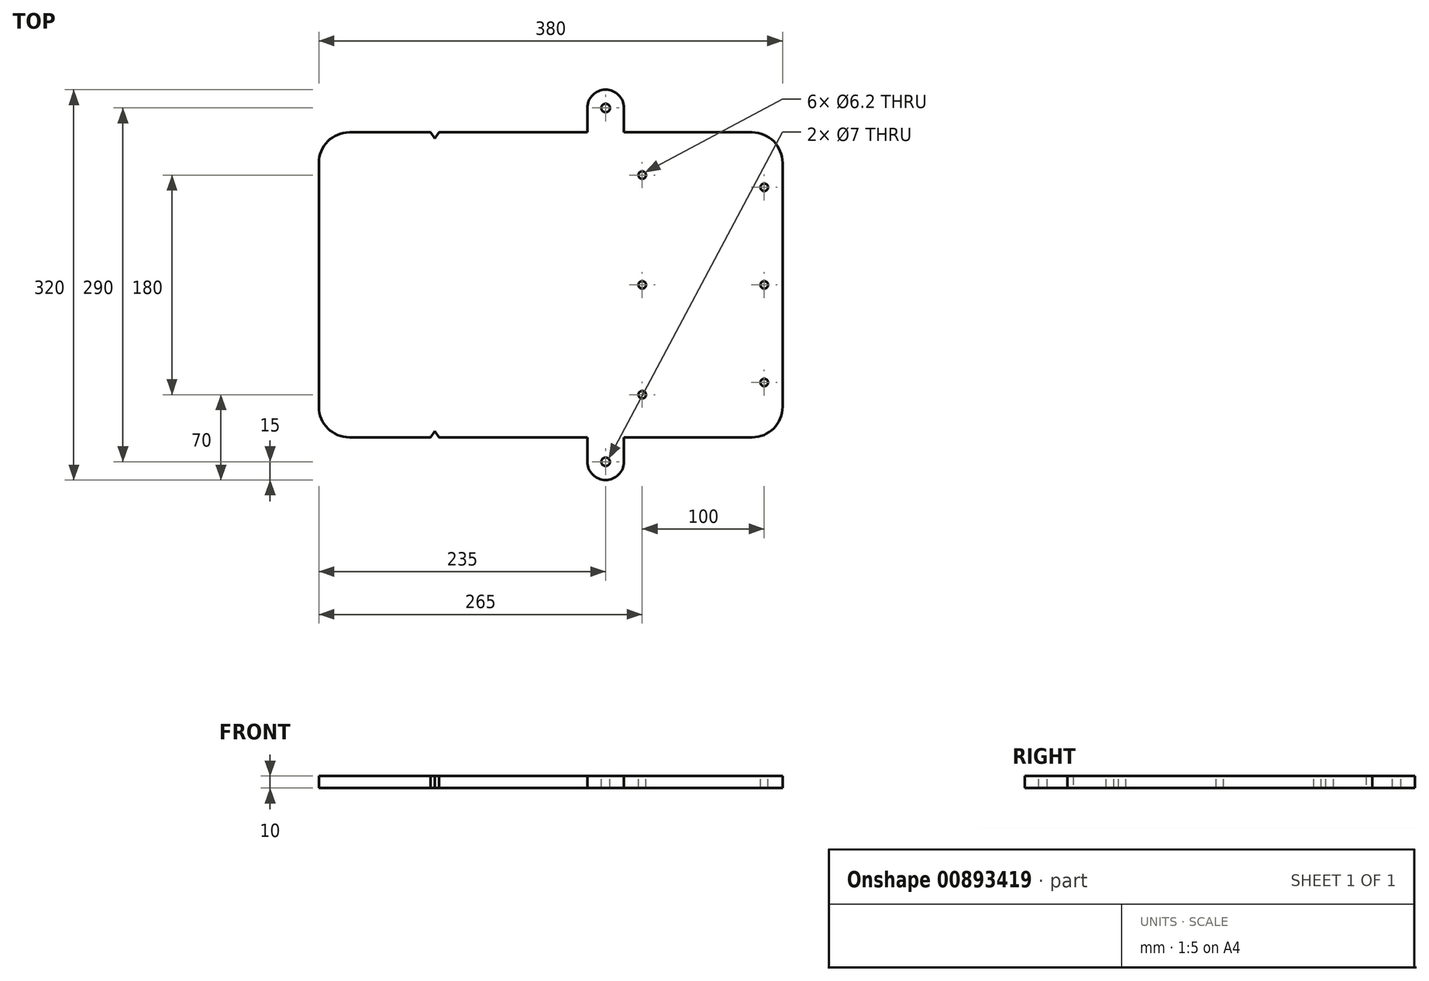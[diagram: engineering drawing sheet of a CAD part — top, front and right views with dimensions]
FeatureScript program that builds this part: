
annotation { "Feature Type Name" : "Feature", "Feature Type Description" : "" }
export const myFeature = defineFeature(function(context is Context, id is Id, definition is map)
    precondition{}
    {
        {
            var Q0;
            Q0=qCreatedBy(makeId("Top.planeOp"),FACE);
            var sketch = newSketch(context, id + "F0", { "sketchPlane" : qUnion([Q0])});
            skLineSegment(sketch, "E0.bottom", {"start": v(25, 0) * mm, "end": v(91.56, 0) * mm});
            skLineSegment(sketch, "E0.top", {"start": v(25, 250) * mm, "end": v(91.56, 250) * mm});
            skLineSegment(sketch, "E0.left", {"start": v(0, 25) * mm, "end": v(0, 225) * mm});
            skLineSegment(sketch, "E0.right", {"start": v(380, 25) * mm, "end": v(380, 225) * mm});
            skLineSegment(sketch, "E1.top", {"start": v(235, 285) * mm, "end": v(235, 285) * mm});
            skLineSegment(sketch, "E1.left", {"start": v(220, 250) * mm, "end": v(220, 270) * mm});
            skLineSegment(sketch, "E1.right", {"start": v(250, 250) * mm, "end": v(250, 270) * mm});
            skLineSegment(sketch, "E2.top", {"start": v(235, -35) * mm, "end": v(235, -35) * mm});
            skLineSegment(sketch, "E2.left", {"start": v(250, 0) * mm, "end": v(250, -20) * mm});
            skLineSegment(sketch, "E2.right", {"start": v(220, 0) * mm, "end": v(220, -20) * mm});
            skLineSegment(sketch, "E3.trimOffspring", {"start": v(250, 250) * mm, "end": v(355, 250) * mm});
            skLineSegment(sketch, "E4.trimOffspring", {"start": v(250, 0) * mm, "end": v(355, 0) * mm});
            skPoint(sketch, "E5.visualSharp", {"position": v(220, 285) * mm});
            skArc(sketch, "E5.filletArc", {"start": v(235, 285) * mm, "mid": v(224.4, 280.6) * mm, "end": v(220, 270) * mm});
            skPoint(sketch, "E6.visualSharp", {"position": v(250, 285) * mm});
            skArc(sketch, "E6.filletArc", {"start": v(250, 270) * mm, "mid": v(245.6, 280.6) * mm, "end": v(235, 285) * mm});
            skPoint(sketch, "E7.visualSharp", {"position": v(220, -35) * mm});
            skArc(sketch, "E7.filletArc", {"start": v(220, -20) * mm, "mid": v(224.4, -30.6) * mm, "end": v(235, -35) * mm});
            skPoint(sketch, "E8.visualSharp", {"position": v(250, -35) * mm});
            skArc(sketch, "E8.filletArc", {"start": v(235, -35) * mm, "mid": v(245.6, -30.6) * mm, "end": v(250, -20) * mm});
            skPoint(sketch, "E9.visualSharp", {"position": v(0, 250) * mm});
            skArc(sketch, "E9.filletArc", {"start": v(25, 250) * mm, "mid": v(7.32, 242.68) * mm, "end": v(0, 225) * mm});
            skPoint(sketch, "E10.visualSharp", {"position": v(0, 0) * mm});
            skArc(sketch, "E10.filletArc", {"start": v(0, 25) * mm, "mid": v(7.32, 7.32) * mm, "end": v(25, 0) * mm});
            skPoint(sketch, "E11.visualSharp", {"position": v(380, 0) * mm});
            skArc(sketch, "E11.filletArc", {"start": v(355, 0) * mm, "mid": v(372.68, 7.32) * mm, "end": v(380, 25) * mm});
            skPoint(sketch, "E12.visualSharp", {"position": v(380, 250) * mm});
            skArc(sketch, "E12.filletArc", {"start": v(380, 225) * mm, "mid": v(372.68, 242.68) * mm, "end": v(355, 250) * mm});
            skLineSegment(sketch, "E13", {"start": v(98.44, 250) * mm, "end": v(95, 245) * mm});
            skLineSegment(sketch, "E14", {"start": v(95, 245) * mm, "end": v(91.56, 250) * mm});
            skLineSegment(sketch, "E15.trimOffspring", {"start": v(98.44, 250) * mm, "end": v(220, 250) * mm});
            skLineSegment(sketch, "E16.MirrorCS", {"start": v(98.44, 0) * mm, "end": v(95, 5) * mm});
            skLineSegment(sketch, "E17.MirrorCS", {"start": v(95, 5) * mm, "end": v(91.56, 0) * mm});
            skLineSegment(sketch, "E18.trimOffspring", {"start": v(98.44, 0) * mm, "end": v(220, 0) * mm});
            skPoint(sketch, "E19.end.orphan", {"position": v(380, 125) * mm});
            skPoint(sketch, "E19.start.orphan", {"position": v(0, 125) * mm});
            skSolve(sketch);
        }
        {
            var Q0;
            Q0=makeQuery(id+"F0.imprint","IMPRINT",FACE,{"disambiguationData":[TD([[makeQuery(id+"F0.imprint","IMPRINT",EDGE,{"derivedFrom":sQuery(id+"F0.wireOp",EDGE,"E0.bottom")}),1.0]])]});
            extrude(context, id + "F1", {"entities" : qUnion([Q0]), "depth" : 10 * mm, "offsetDistance" : 25 * mm});
        }
        {
            var Q0;
            Q0=makeQuery(id+"F1.opExtrude","CAP_FACE",FACE,{"disambiguationData":[OSD([sQuery(id+"F0.wireOp",EDGE,"E0.bottom"),sQuery(id+"F0.wireOp",EDGE,"E0.top"),sQuery(id+"F0.wireOp",EDGE,"E0.left"),sQuery(id+"F0.wireOp",EDGE,"E0.right"),sQuery(id+"F0.wireOp",EDGE,"E1.left"),sQuery(id+"F0.wireOp",EDGE,"E1.right"),sQuery(id+"F0.wireOp",EDGE,"E2.left"),sQuery(id+"F0.wireOp",EDGE,"E2.right"),sQuery(id+"F0.wireOp",EDGE,"E3.trimOffspring"),sQuery(id+"F0.wireOp",EDGE,"E4.trimOffspring"),sQuery(id+"F0.wireOp",EDGE,"E5.filletArc"),sQuery(id+"F0.wireOp",EDGE,"E6.filletArc"),sQuery(id+"F0.wireOp",EDGE,"E7.filletArc"),sQuery(id+"F0.wireOp",EDGE,"E8.filletArc"),sQuery(id+"F0.wireOp",EDGE,"E9.filletArc"),sQuery(id+"F0.wireOp",EDGE,"E10.filletArc"),sQuery(id+"F0.wireOp",EDGE,"E11.filletArc"),sQuery(id+"F0.wireOp",EDGE,"E12.filletArc")])],"isStart":false});
            var sketch = newSketch(context, id + "F2", { "sketchPlane" : qUnion([Q0])});
            skCircle(sketch, "E20", {"center": v(235, 270) * mm, "radius": 3.5 * mm});
            skCircle(sketch, "E21", {"center": v(235, -20) * mm, "radius": 3.5 * mm});
            skSolve(sketch);
        }
        {
            var Q0;
            Q0=makeQuery(id+"F2.imprint","IMPRINT",FACE,{"disambiguationData":[TD([[makeQuery(id+"F2.imprint","IMPRINT",EDGE,{"derivedFrom":sQuery(id+"F2.wireOp",EDGE,"E21")}),1.0]])]});
            var Q1;
            Q1=makeQuery(id+"F2.imprint","IMPRINT",FACE,{"disambiguationData":[TD([[makeQuery(id+"F2.imprint","IMPRINT",EDGE,{"derivedFrom":sQuery(id+"F2.wireOp",EDGE,"E20")}),1.0]])]});
            extrude(context, id + "F3", {"entities" : qUnion([Q0, Q1]), "operationType" : NewBodyOperationType.REMOVE, "oppositeDirection" : true, "depth" : 25 * mm, "offsetDistance" : 25 * mm});
        }
        {
            var Q0;
            Q0=makeQuery(id+"F1.opExtrude","CAP_FACE",FACE,{"disambiguationData":[OSD([sQuery(id+"F0.wireOp",EDGE,"E0.bottom"),sQuery(id+"F0.wireOp",EDGE,"E0.top"),sQuery(id+"F0.wireOp",EDGE,"E0.left"),sQuery(id+"F0.wireOp",EDGE,"E0.right"),sQuery(id+"F0.wireOp",EDGE,"E1.left"),sQuery(id+"F0.wireOp",EDGE,"E1.right"),sQuery(id+"F0.wireOp",EDGE,"E2.left"),sQuery(id+"F0.wireOp",EDGE,"E2.right"),sQuery(id+"F0.wireOp",EDGE,"E3.trimOffspring"),sQuery(id+"F0.wireOp",EDGE,"E4.trimOffspring"),sQuery(id+"F0.wireOp",EDGE,"E5.filletArc"),sQuery(id+"F0.wireOp",EDGE,"E6.filletArc"),sQuery(id+"F0.wireOp",EDGE,"E7.filletArc"),sQuery(id+"F0.wireOp",EDGE,"E8.filletArc"),sQuery(id+"F0.wireOp",EDGE,"E9.filletArc"),sQuery(id+"F0.wireOp",EDGE,"E10.filletArc"),sQuery(id+"F0.wireOp",EDGE,"E11.filletArc"),sQuery(id+"F0.wireOp",EDGE,"E12.filletArc"),sQuery(id+"F0.wireOp",EDGE,"E13"),sQuery(id+"F0.wireOp",EDGE,"E14"),sQuery(id+"F0.wireOp",EDGE,"E15.trimOffspring"),sQuery(id+"F0.wireOp",EDGE,"E16.MirrorCS"),sQuery(id+"F0.wireOp",EDGE,"E17.MirrorCS"),sQuery(id+"F0.wireOp",EDGE,"E18.trimOffspring")])],"isStart":false});
            var sketch = newSketch(context, id + "F4", { "sketchPlane" : qUnion([Q0])});
            skCircle(sketch, "E22", {"center": v(365, 125) * mm, "radius": 3.1 * mm});
            skCircle(sketch, "E23", {"center": v(365, 45) * mm, "radius": 3.1 * mm});
            skCircle(sketch, "E24", {"center": v(265, 215) * mm, "radius": 3.1 * mm});
            skCircle(sketch, "E25", {"center": v(265, 125) * mm, "radius": 3.1 * mm});
            skCircle(sketch, "E26", {"center": v(265, 35) * mm, "radius": 3.1 * mm});
            skCircle(sketch, "E27", {"center": v(365, 205) * mm, "radius": 3.1 * mm});
            skSolve(sketch);
        }
        {
            var Q0;
            Q0=makeQuery(id+"F4.imprint","IMPRINT",FACE,{"disambiguationData":[TD([[makeQuery(id+"F4.imprint","IMPRINT",EDGE,{"derivedFrom":sQuery(id+"F4.wireOp",EDGE,"E24")}),1.0]])]});
            var Q1;
            Q1=makeQuery(id+"F4.imprint","IMPRINT",FACE,{"disambiguationData":[TD([[makeQuery(id+"F4.imprint","IMPRINT",EDGE,{"derivedFrom":sQuery(id+"F4.wireOp",EDGE,"E25")}),1.0]])]});
            var Q2;
            Q2=makeQuery(id+"F4.imprint","IMPRINT",FACE,{"disambiguationData":[TD([[makeQuery(id+"F4.imprint","IMPRINT",EDGE,{"derivedFrom":sQuery(id+"F4.wireOp",EDGE,"E26")}),1.0]])]});
            var Q3;
            Q3=makeQuery(id+"F4.imprint","IMPRINT",FACE,{"disambiguationData":[TD([[makeQuery(id+"F4.imprint","IMPRINT",EDGE,{"derivedFrom":sQuery(id+"F4.wireOp",EDGE,"E23")}),1.0]])]});
            var Q4;
            Q4=makeQuery(id+"F4.imprint","IMPRINT",FACE,{"disambiguationData":[TD([[makeQuery(id+"F4.imprint","IMPRINT",EDGE,{"derivedFrom":sQuery(id+"F4.wireOp",EDGE,"E22")}),1.0]])]});
            var Q5;
            Q5=makeQuery(id+"F4.imprint","IMPRINT",FACE,{"disambiguationData":[TD([[makeQuery(id+"F4.imprint","IMPRINT",EDGE,{"derivedFrom":sQuery(id+"F4.wireOp",EDGE,"E27")}),1.0]])]});
            extrude(context, id + "F5", {"entities" : qUnion([Q0, Q1, Q2, Q3, Q4, Q5]), "operationType" : NewBodyOperationType.REMOVE, "oppositeDirection" : true, "depth" : 25 * mm, "offsetDistance" : 25 * mm});
        }
    });
